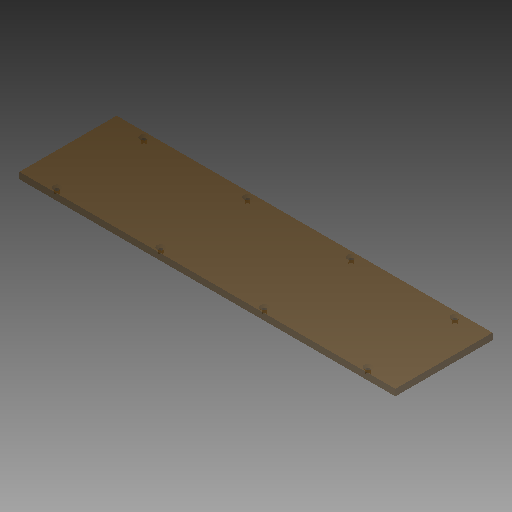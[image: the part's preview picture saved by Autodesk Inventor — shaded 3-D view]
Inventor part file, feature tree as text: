
AUTODESK INVENTOR PART (.ipt)
format: ipt  version: 2018 (Build 220112000, 112)  size: 99,328 bytes
history: native  units: mm
features: extrude x1, hole x1, pattern_linear x1
ambient origin geometry x8: Origin, YZ Plane, XZ Plane, XY Plane, X Axis, Y Axis, Z Axis, Center Point
bodies: Volumenkörper1 (feature_tree)
feature tree (3):
  extrude  "Extrusion1"  Depth=290.0mm
  hole  "Bohrung1"  [1 undecoded]
  pattern_linear  "Rechteckige Anordnung1"  Spacing1=5.0mm  [1 undecoded]
note: 2 required parameter values undecoded (feature->parameter linkage not recoverable at this tier; creation-order binding heuristic only, values carry confidence <= 0.55)
